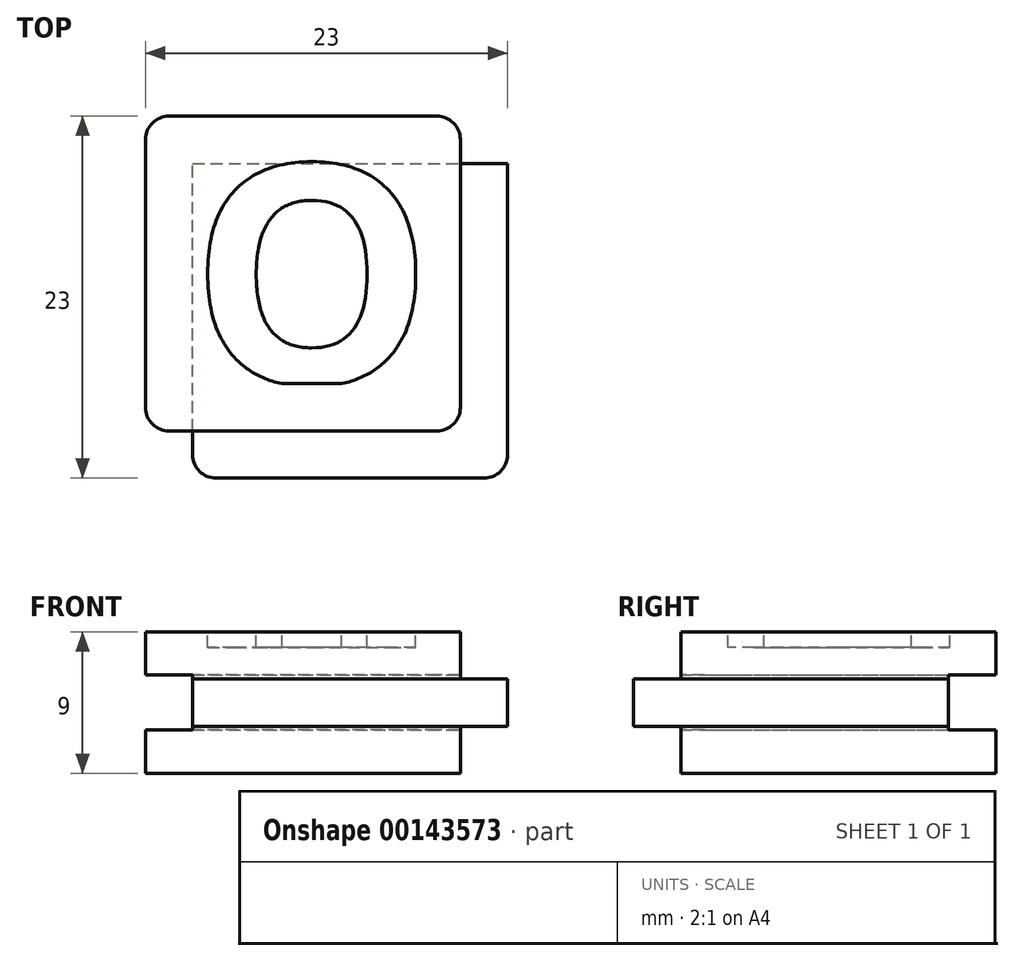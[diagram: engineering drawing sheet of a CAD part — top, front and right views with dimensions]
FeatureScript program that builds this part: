
annotation { "Feature Type Name" : "Feature", "Feature Type Description" : "" }
export const myFeature = defineFeature(function(context is Context, id is Id, definition is map)
    precondition{}
    {
        {
            var Q0;
            Q0=qCreatedBy(makeId("Front.planeOp"),FACE);
            var sketch = newSketch(context, id + "F0", { "sketchPlane" : qUnion([Q0])});
            skLineSegment(sketch, "E0.bottom", {"start": v(10, 4.5) * mm, "end": v(-10, 4.5) * mm});
            skLineSegment(sketch, "E0.top", {"start": v(10, -4.5) * mm, "end": v(-10, -4.5) * mm});
            skLineSegment(sketch, "E0.left", {"start": v(10, 4.5) * mm, "end": v(10, -4.5) * mm});
            skLineSegment(sketch, "E0.right", {"start": v(-10, 4.5) * mm, "end": v(-10, -4.5) * mm});
            skPoint(sketch, "E0.middle", {"position": v(0, 0) * mm});
            skLineSegment(sketch, "E1.bottom", {"start": v(13, 1.5) * mm, "end": v(7, 1.5) * mm});
            skLineSegment(sketch, "E1.top", {"start": v(13, -1.5) * mm, "end": v(7, -1.5) * mm});
            skLineSegment(sketch, "E1.left", {"start": v(13, 1.5) * mm, "end": v(13, -1.5) * mm});
            skLineSegment(sketch, "E1.right", {"start": v(7, 1.5) * mm, "end": v(7, -1.5) * mm});
            skPoint(sketch, "E1.middle", {"position": v(10, 0) * mm});
            skLineSegment(sketch, "E2.bottom", {"start": v(7, 1.5) * mm, "end": v(-7, 1.5) * mm});
            skLineSegment(sketch, "E2.top", {"start": v(7, -1.5) * mm, "end": v(-7, -1.5) * mm});
            skLineSegment(sketch, "E2.right", {"start": v(-7, 1.5) * mm, "end": v(-7, -1.5) * mm});
            skLineSegment(sketch, "E3.bottom", {"start": v(-7, -1.5) * mm, "end": v(-10, -1.5) * mm});
            skLineSegment(sketch, "E3.top", {"start": v(-7, 1.5) * mm, "end": v(-10, 1.5) * mm});
            skLineSegment(sketch, "E3.left", {"start": v(-7, -1.5) * mm, "end": v(-7, 1.5) * mm});
            skLineSegment(sketch, "E3.right", {"start": v(-10, -1.5) * mm, "end": v(-10, 1.5) * mm});
            skSolve(sketch);
        }
        {
            var Q0;
            {var subQ5=sQuery(id+"F0.wireOp",EDGE,"E0.bottom");Q0=makeQuery(id+"F0.imprint","IMPRINT",FACE,{"disambiguationData":[TD([[makeQuery(id+"F0.imprint","IMPRINT",EDGE,{"derivedFrom":subQ5}),1.0]])]});}
            var Q1;
            Q1=makeQuery(id+"F0.imprint","IMPRINT",FACE,{"disambiguationData":[TD([[makeQuery(id+"F0.imprint","IMPRINT",EDGE,{"derivedFrom":sQuery(id+"F0.wireOp",EDGE,"E2.bottom")}),1.0]])]});
            var Q2;
            {var subQ5=sQuery(id+"F0.wireOp",EDGE,"E1.left");Q2=makeQuery(id+"F0.imprint","IMPRINT",FACE,{"disambiguationData":[TD([[makeQuery(id+"F0.imprint","IMPRINT",EDGE,{"derivedFrom":subQ5}),-1.0]])]});}
            var Q3;
            {var subQ5=sQuery(id+"F0.wireOp",EDGE,"E1.right");Q3=makeQuery(id+"F0.imprint","IMPRINT",FACE,{"disambiguationData":[TD([[makeQuery(id+"F0.imprint","IMPRINT",EDGE,{"derivedFrom":subQ5}),1.0]])]});}
            var Q4;
            Q4=makeQuery(id+"F0.imprint","IMPRINT",FACE,{"disambiguationData":[TD([[makeQuery(id+"F0.imprint","IMPRINT",EDGE,{"derivedFrom":sQuery(id+"F0.wireOp",EDGE,"E3.bottom")}),-1.0]])]});
            var Q5;
            {var subQ5=sQuery(id+"F0.wireOp",EDGE,"E0.top");Q5=makeQuery(id+"F0.imprint","IMPRINT",FACE,{"disambiguationData":[TD([[makeQuery(id+"F0.imprint","IMPRINT",EDGE,{"derivedFrom":subQ5}),-1.0]])]});}
            extrude(context, id + "F1", {"entities" : qUnion([Q0, Q1, Q2, Q3, Q4, Q5]), "oppositeDirection" : true, "depth" : 20 * mm});
        }
        {
            var Q0;
            Q0=makeQuery(id+"F0.imprint","IMPRINT",FACE,{"disambiguationData":[TD([[makeQuery(id+"F0.imprint","IMPRINT",EDGE,{"derivedFrom":sQuery(id+"F0.wireOp",EDGE,"E3.bottom")}),-1.0]])]});
            var Q1;
            Q1=makeQuery(id+"F0.imprint","IMPRINT",FACE,{"disambiguationData":[TD([[makeQuery(id+"F0.imprint","IMPRINT",EDGE,{"derivedFrom":sQuery(id+"F0.wireOp",EDGE,"E2.bottom")}),1.0]])]});
            var Q2;
            {var subQ5=sQuery(id+"F0.wireOp",EDGE,"E1.right");Q2=makeQuery(id+"F0.imprint","IMPRINT",FACE,{"disambiguationData":[TD([[makeQuery(id+"F0.imprint","IMPRINT",EDGE,{"derivedFrom":subQ5}),1.0]])]});}
            var Q3;
            {var subQ5=sQuery(id+"F0.wireOp",EDGE,"E1.left");Q3=makeQuery(id+"F0.imprint","IMPRINT",FACE,{"disambiguationData":[TD([[makeQuery(id+"F0.imprint","IMPRINT",EDGE,{"derivedFrom":subQ5}),-1.0]])]});}
            extrude(context, id + "F2", {"entities" : qUnion([Q0, Q1, Q2, Q3]), "operationType" : NewBodyOperationType.ADD, "depth" : 3 * mm});
        }
        {
            var Q0;
            {var subQ0=sQuery(id+"F0.wireOp",EDGE,"E1.left");Q0=makeQuery(id+"F2.boolean.opBoolean","MERGE",FACE,{"derivedFrom":[makeQuery(id+"F1.opExtrude","SWEPT_FACE",FACE,{"disambiguationData":[OSD([subQ0])]}),makeQuery(id+"F2.opExtrude","SWEPT_FACE",FACE,{"disambiguationData":[OSD([subQ0])]})]});}
            var sketch = newSketch(context, id + "F3", { "sketchPlane" : qUnion([Q0])});
            skLineSegment(sketch, "E4.bottom", {"start": v(23, 1.75) * mm, "end": v(17, 1.75) * mm});
            skLineSegment(sketch, "E4.top", {"start": v(23, -1.75) * mm, "end": v(17, -1.75) * mm});
            skLineSegment(sketch, "E4.left", {"start": v(23, 1.75) * mm, "end": v(23, -1.75) * mm});
            skLineSegment(sketch, "E4.right", {"start": v(17, 1.75) * mm, "end": v(17, -1.75) * mm});
            skPoint(sketch, "E4.middle", {"position": v(20, 0) * mm});
            skSolve(sketch);
        }
        {
            var Q0;
            {var subQ1=sQuery(id+"F3.wireOp",EDGE,"E4.bottom");Q0=makeQuery(id+"F3.imprint","IMPRINT",FACE,{"disambiguationData":[TD([[makeQuery(id+"F3.imprint","IMPRINT",EDGE,{"derivedFrom":subQ1}),1.0]])]});}
            var Q1;
            {var subQ1=sQuery(id+"F0.wireOp",EDGE,"E1.left");var subQ8=makeQuery(id+"F1.opExtrude","CAP_EDGE",EDGE,{"disambiguationData":[OSD([subQ1])],"isStart":false});Q1=makeQuery(id+"F3.imprint","IMPRINT",FACE,{"disambiguationData":[TD([[makeQuery(id+"F3.imprint","IMPRINT",EDGE,{"derivedFrom":subQ8}),-1.0]])]});}
            extrude(context, id + "F4", {"entities" : qUnion([Q0, Q1]), "operationType" : NewBodyOperationType.REMOVE, "oppositeDirection" : true, "depth" : 100 * mm});
        }
        {
            var Q0;
            Q0=makeQuery(id+"F4.boolean.opBoolean","COPY",FACE,{"derivedFrom":makeQuery(id+"F4.opExtrude","SWEPT_FACE",FACE,{"disambiguationData":[OSD([sQuery(id+"F3.wireOp",EDGE,"E4.right")])]})});
            var sketch = newSketch(context, id + "F5", { "sketchPlane" : qUnion([Q0])});
            skLineSegment(sketch, "E5.bottom", {"start": v(13, 1.75) * mm, "end": v(7, 1.75) * mm});
            skLineSegment(sketch, "E5.top", {"start": v(13, -1.75) * mm, "end": v(7, -1.75) * mm});
            skLineSegment(sketch, "E5.left", {"start": v(13, 1.75) * mm, "end": v(13, -1.75) * mm});
            skLineSegment(sketch, "E5.right", {"start": v(7, 1.75) * mm, "end": v(7, -1.75) * mm});
            skPoint(sketch, "E5.middle", {"position": v(10, 0) * mm});
            skSolve(sketch);
        }
        {
            var Q0;
            {var subQ3=sQuery(id+"F5.wireOp",EDGE,"E5.left");Q0=makeQuery(id+"F5.imprint","IMPRINT",FACE,{"disambiguationData":[TD([[makeQuery(id+"F5.imprint","IMPRINT",EDGE,{"derivedFrom":subQ3}),-1.0]])]});}
            var Q1;
            {var subQ4=sQuery(id+"F5.wireOp",EDGE,"E5.right");Q1=makeQuery(id+"F5.imprint","IMPRINT",FACE,{"disambiguationData":[TD([[makeQuery(id+"F5.imprint","IMPRINT",EDGE,{"derivedFrom":subQ4}),1.0]])]});}
            extrude(context, id + "F6", {"entities" : qUnion([Q0, Q1]), "operationType" : NewBodyOperationType.REMOVE, "oppositeDirection" : true, "depth" : 100 * mm});
        }
        {
            var Q0;
            Q0=makeQuery(id+"F6.boolean.opBoolean","INTERSECT",EDGE,{"derivedFrom":[makeQuery(id+"F2.opExtrude","CAP_FACE",FACE,{"disambiguationData":[OSD([sQuery(id+"F0.wireOp",EDGE,"E1.bottom"),sQuery(id+"F0.wireOp",EDGE,"E1.top"),sQuery(id+"F0.wireOp",EDGE,"E1.left"),sQuery(id+"F0.wireOp",EDGE,"E2.bottom"),sQuery(id+"F0.wireOp",EDGE,"E2.top"),sQuery(id+"F0.wireOp",EDGE,"E3.bottom"),sQuery(id+"F0.wireOp",EDGE,"E3.top"),sQuery(id+"F0.wireOp",EDGE,"E3.right")])],"isStart":false}),makeQuery(id+"F6.opExtrude","SWEPT_FACE",FACE,{"disambiguationData":[OSD([sQuery(id+"F5.wireOp",EDGE,"E5.right")])]})]});
            var Q1;
            Q1=makeQuery(id+"F2.opExtrude","CAP_EDGE",EDGE,{"disambiguationData":[OSD([sQuery(id+"F0.wireOp",EDGE,"E1.left")])],"isStart":false});
            var Q2;
            {var subQ0=sQuery(id+"F0.wireOp",EDGE,"E0.left");Q2=makeQuery(id+"F1.opExtrude","CAP_EDGE",EDGE,{"disambiguationData":[OSD([subQ0]),TDD([makeQuery(id+"F0.imprint","IMPRINT",EDGE,{"disambiguationData":[TD([[makeQuery(id+"F0.imprint","INTERSECT",VERTEX,{"derivedFrom":[sQuery(id+"F0.wireOp",EDGE,"E0.bottom"),subQ0]}),-1.0]])],"derivedFrom":subQ0})])],"isStart":true});}
            var Q3;
            {var subQ0=sQuery(id+"F0.wireOp",EDGE,"E0.left");Q3=makeQuery(id+"F1.opExtrude","CAP_EDGE",EDGE,{"disambiguationData":[OSD([subQ0]),TDD([makeQuery(id+"F0.imprint","IMPRINT",EDGE,{"disambiguationData":[TD([[makeQuery(id+"F0.imprint","INTERSECT",VERTEX,{"derivedFrom":[sQuery(id+"F0.wireOp",EDGE,"E0.top"),subQ0]}),1.0]])],"derivedFrom":subQ0})])],"isStart":true});}
            var Q4;
            {var subQ0=sQuery(id+"F0.wireOp",EDGE,"E3.right");var subQ1=sQuery(id+"F0.wireOp",EDGE,"E0.right");var subQ3=sQuery(id+"F0.wireOp",EDGE,"E0.top");Q4=makeQuery(id+"F2.boolean.opBoolean","SPLIT",EDGE,{"disambiguationData":[TD([makeQuery(id+"F1.opExtrude","SWEPT_FACE",FACE,{"disambiguationData":[OSD([subQ3])]})])],"derivedFrom":makeQuery(id+"F1.opExtrude","CAP_EDGE",EDGE,{"disambiguationData":[OSD([subQ1,subQ0])],"isStart":true})});}
            var Q5;
            {var subQ1=sQuery(id+"F0.wireOp",EDGE,"E3.right");var subQ2=sQuery(id+"F0.wireOp",EDGE,"E0.right");var subQ3=sQuery(id+"F0.wireOp",EDGE,"E0.bottom");Q5=makeQuery(id+"F2.boolean.opBoolean","SPLIT",EDGE,{"disambiguationData":[TD([makeQuery(id+"F1.opExtrude","SWEPT_FACE",FACE,{"disambiguationData":[OSD([subQ3])]})])],"derivedFrom":makeQuery(id+"F1.opExtrude","CAP_EDGE",EDGE,{"disambiguationData":[OSD([subQ2,subQ1])],"isStart":true})});}
            var Q6;
            Q6=makeQuery(id+"F6.boolean.opBoolean","COPY",EDGE,{"derivedFrom":makeQuery(id+"F6.opExtrude","CAP_EDGE",EDGE,{"disambiguationData":[OSD([sQuery(id+"F5.wireOp",EDGE,"E5.right")])],"isStart":true})});
            var Q7;
            {var subQ0=sQuery(id+"F0.wireOp",EDGE,"E3.right");var subQ1=sQuery(id+"F0.wireOp",EDGE,"E0.right");var subQ2=sQuery(id+"F0.wireOp",EDGE,"E0.bottom");Q7=makeQuery(id+"F4.boolean.opBoolean","SPLIT",EDGE,{"disambiguationData":[TD([makeQuery(id+"F1.opExtrude","SWEPT_FACE",FACE,{"disambiguationData":[OSD([subQ2])]})])],"derivedFrom":makeQuery(id+"F1.opExtrude","CAP_EDGE",EDGE,{"disambiguationData":[OSD([subQ1,subQ0])],"isStart":false})});}
            var Q8;
            {var subQ0=sQuery(id+"F0.wireOp",EDGE,"E3.right");var subQ1=sQuery(id+"F0.wireOp",EDGE,"E0.right");var subQ2=sQuery(id+"F0.wireOp",EDGE,"E0.top");Q8=makeQuery(id+"F4.boolean.opBoolean","SPLIT",EDGE,{"disambiguationData":[TD([makeQuery(id+"F1.opExtrude","SWEPT_FACE",FACE,{"disambiguationData":[OSD([subQ2])]})])],"derivedFrom":makeQuery(id+"F1.opExtrude","CAP_EDGE",EDGE,{"disambiguationData":[OSD([subQ1,subQ0])],"isStart":false})});}
            var Q9;
            Q9=makeQuery(id+"F4.boolean.opBoolean","COPY",EDGE,{"derivedFrom":makeQuery(id+"F4.opExtrude","CAP_EDGE",EDGE,{"disambiguationData":[OSD([sQuery(id+"F3.wireOp",EDGE,"E4.right")])],"isStart":true})});
            var Q10;
            {var subQ0=sQuery(id+"F0.wireOp",EDGE,"E0.left");Q10=makeQuery(id+"F1.opExtrude","CAP_EDGE",EDGE,{"disambiguationData":[OSD([subQ0]),TDD([makeQuery(id+"F0.imprint","IMPRINT",EDGE,{"disambiguationData":[TD([[makeQuery(id+"F0.imprint","INTERSECT",VERTEX,{"derivedFrom":[sQuery(id+"F0.wireOp",EDGE,"E0.bottom"),subQ0]}),-1.0]])],"derivedFrom":subQ0})])],"isStart":false});}
            var Q11;
            {var subQ0=sQuery(id+"F0.wireOp",EDGE,"E0.left");Q11=makeQuery(id+"F1.opExtrude","CAP_EDGE",EDGE,{"disambiguationData":[OSD([subQ0]),TDD([makeQuery(id+"F0.imprint","IMPRINT",EDGE,{"disambiguationData":[TD([[makeQuery(id+"F0.imprint","INTERSECT",VERTEX,{"derivedFrom":[sQuery(id+"F0.wireOp",EDGE,"E0.top"),subQ0]}),1.0]])],"derivedFrom":subQ0})])],"isStart":false});}
            fillet(context, id + "F7", {"entities" : qUnion([Q0, Q1, Q2, Q3, Q4, Q5, Q6, Q7, Q8, Q9, Q10, Q11]), "radius" : 1.5 * mm, "tangentPropagation" : true, "allowEdgeOverflow" : false});
        }
        {
            var Q0;
            Q0=makeQuery(id+"F1.opExtrude","SWEPT_FACE",FACE,{"disambiguationData":[OSD([sQuery(id+"F0.wireOp",EDGE,"E0.bottom")])]});
            var sketch = newSketch(context, id + "F8", { "sketchPlane" : qUnion([Q0])});
            skText(sketch, "E6", { "text": "O", "fontName": "OpenSans-Bold.ttf"});
            skLineSegment(sketch, "E7.0", {"start": v(12.32, 3) * mm, "end": v(-11.07, 3) * mm});
            const initialGuessF8  = {"E6": [-0.00718, 0.003, 1, 0, 0.014]};
            skSetInitialGuess(sketch, initialGuessF8);
            skSolve(sketch);
        }
        {
            var Q0;
            Q0=makeQuery(id+"F8.imprint","IMPRINT",FACE,{"disambiguationData":[TD([[makeQuery(id+"F8.imprint","IMPRINT",EDGE,{"derivedFrom":sQuery(id+"F8.wireOp",EDGE,"E6.sketch_text.stroke-0")}),-1.0]])]});
            extrude(context, id + "F9", {"entities" : qUnion([Q0]), "operationType" : NewBodyOperationType.REMOVE, "oppositeDirection" : true, "depth" : 1 * mm});
        }
    });
